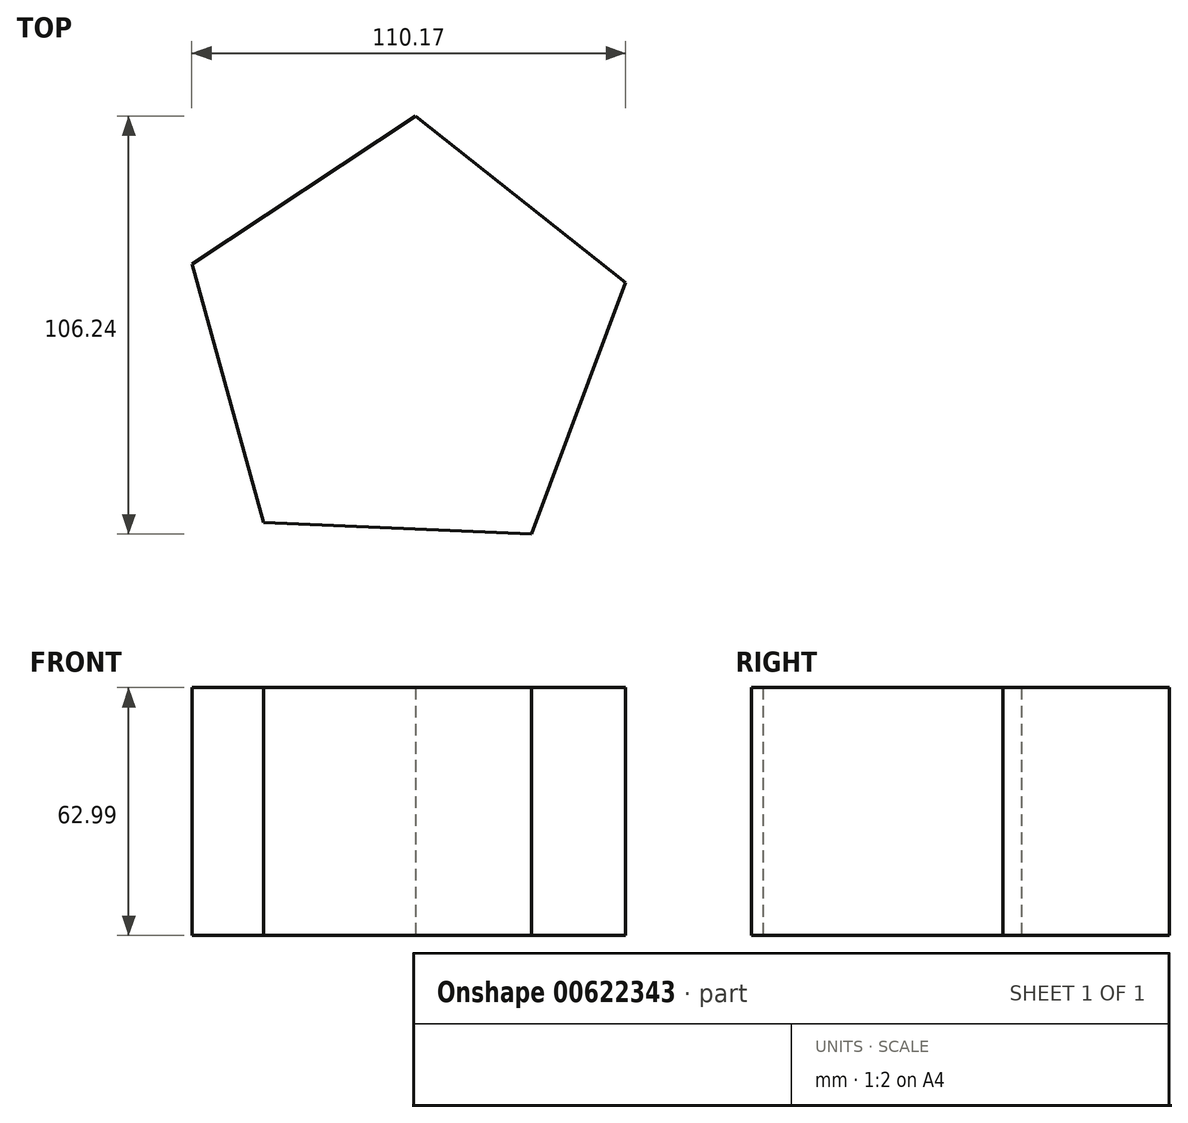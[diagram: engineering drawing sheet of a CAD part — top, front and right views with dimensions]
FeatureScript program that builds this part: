
annotation { "Feature Type Name" : "Feature", "Feature Type Description" : "" }
export const myFeature = defineFeature(function(context is Context, id is Id, definition is map)
    precondition{}
    {
        {
            var Q0;
            Q0=qCreatedBy(makeId("Top.planeOp"),FACE);
            var sketch = newSketch(context, id + "F0", { "sketchPlane" : qUnion([Q0])});
            skCircle(sketch, "E0.cCircle", {"center": v(0, 0) * mm, "radius": 46.9 * mm, "construction": true});
            skLineSegment(sketch, "E0.0", {"start": v(-54.32, 20.26) * mm, "end": v(2.49, 57.92) * mm});
            skLineSegment(sketch, "E0.1", {"start": v(2.49, 57.92) * mm, "end": v(55.85, 15.53) * mm});
            skLineSegment(sketch, "E0.2", {"start": v(55.85, 15.53) * mm, "end": v(32.03, -48.32) * mm});
            skLineSegment(sketch, "E0.3", {"start": v(32.03, -48.32) * mm, "end": v(-36.06, -45.4) * mm});
            skLineSegment(sketch, "E0.4", {"start": v(-36.06, -45.4) * mm, "end": v(-54.32, 20.26) * mm});
            skPoint(sketch, "E0.0.midPoint", {"position": v(-25.92, 39.1) * mm});
            skSolve(sketch);
        }
        {
            var Q0;
            Q0=makeQuery(id+"F0.imprint","IMPRINT",FACE,{"disambiguationData":[TD([[makeQuery(id+"F0.imprint","IMPRINT",EDGE,{"derivedFrom":sQuery(id+"F0.wireOp",EDGE,"E0.0")}),-1.0]])]});
            extrude(context, id + "F1", {"entities" : qUnion([Q0]), "depth" : 63 * mm, "offsetDistance" : 25.4 * mm});
        }
    });
